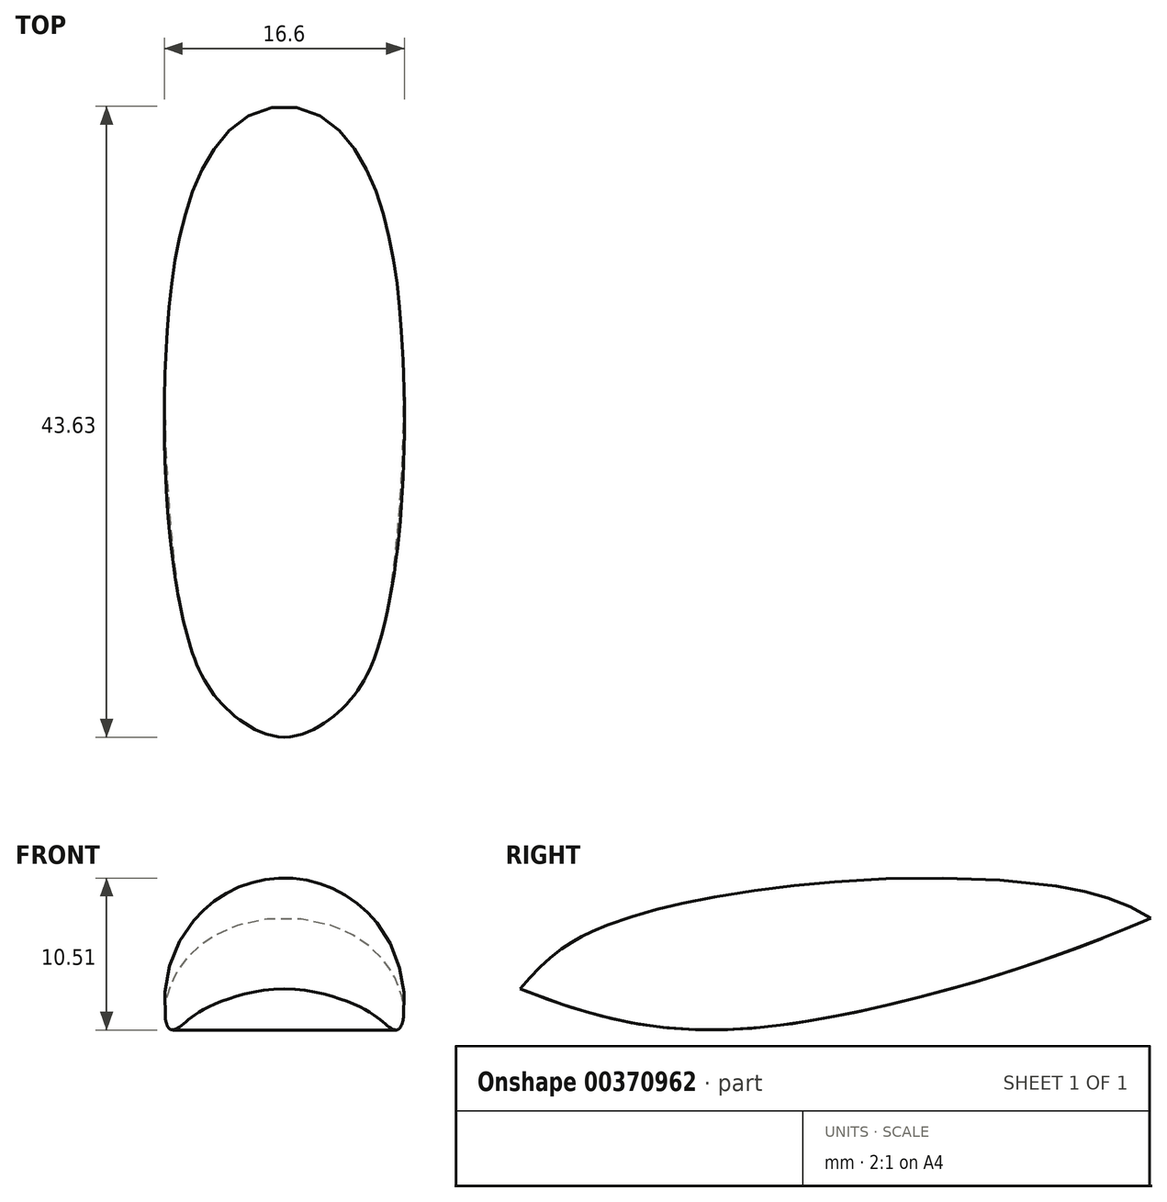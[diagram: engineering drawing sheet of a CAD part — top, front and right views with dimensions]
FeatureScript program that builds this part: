
annotation { "Feature Type Name" : "Feature", "Feature Type Description" : "" }
export const myFeature = defineFeature(function(context is Context, id is Id, definition is map)
    precondition{}
    {
        {
            var Q0;
            Q0=qCreatedBy(makeId("Right.planeOp"),FACE);
            var sketch = newSketch(context, id + "F0", { "sketchPlane" : qUnion([Q0])});
            skLineSegment(sketch, "E0", {"start": v(-61.43, 0) * mm, "end": v(63.71, 0) * mm});
            skLineSegment(sketch, "E1", {"start": v(63.71, 0) * mm, "end": v(63.71, 21.98) * mm});
            skCircle(sketch, "E2", {"center": v(-32.12, 0) * mm, "radius": 12 * mm});
            skCircle(sketch, "E3", {"center": v(39.07, 2) * mm, "radius": 12 * mm});
            skFitSpline(sketch, "E4", {"points": [v(-61.43, 0) * mm, v(-34.2, 19.3) * mm, v(-22.85, 20.07) * mm, v(-9.5, 15.15) * mm, v(4.65, 13.09) * mm, v(29.55, 19.53) * mm, v(44.48, 23.8) * mm, v(63.71, 21.98) * mm], "startDerivative": vector(151.63, 145.86) * mm, "endDerivative": vector(14.11, 0) * mm});
            skSolve(sketch);
        }
        {
            var Q0;
            Q0=qCreatedBy(makeId("Top.planeOp"),FACE);
            cPlane(context, id + "F1", {"entities" : qUnion([Q0]), "cplaneType" : CPlaneType.OFFSET, "offset" : 3 * mm, "width" : 150 * mm, "height" : 150 * mm});
        }
        {
            var Q0;
            {var subQ0=sQuery(id+"F0.wireOp",EDGE,"E1");Q0=makeQuery(id+"F0.imprint","IMPRINT",FACE,{"disambiguationData":[TD([[makeQuery(id+"F0.imprint","IMPRINT",EDGE,{"derivedFrom":subQ0}),1.0]])]});}
            var Q1;
            {var subQ0=sQuery(id+"F0.wireOp",EDGE,"E2");var subQ1=sQuery(id+"F0.wireOp",EDGE,"E0");var subQ2=makeQuery(id+"F0.imprint","INTERSECT",VERTEX,{"disambiguationData":[OD(0.0)],"derivedFrom":[subQ1,subQ0]});Q1=makeQuery(id+"F0.imprint","IMPRINT",FACE,{"disambiguationData":[TD([[makeQuery(id+"F0.imprint","IMPRINT",EDGE,{"disambiguationData":[TD([[subQ2,-1.0]])],"derivedFrom":subQ1}),1.0]])]});}
            var Q2;
            {var subQ0=sQuery(id+"F0.wireOp",EDGE,"E3");var subQ1=sQuery(id+"F0.wireOp",EDGE,"E0");var subQ2=makeQuery(id+"F0.imprint","INTERSECT",VERTEX,{"disambiguationData":[OD(0.0)],"derivedFrom":[subQ1,subQ0]});Q2=makeQuery(id+"F0.imprint","IMPRINT",FACE,{"disambiguationData":[TD([[makeQuery(id+"F0.imprint","IMPRINT",EDGE,{"disambiguationData":[TD([[subQ2,-1.0]])],"derivedFrom":subQ1}),1.0]])]});}
            extrude(context, id + "F2", {"entities" : qUnion([Q0, Q1, Q2]), "endBound" : BoundingType.SYMMETRIC, "depth" : 60 * mm});
        }
        {
            var Q0;
            Q0=qCreatedBy(makeId("Right.planeOp"),FACE);
            var sketch = newSketch(context, id + "F3", { "sketchPlane" : qUnion([Q0])});
            skFitSpline(sketch, "E5", {"points": [v(-15.16, 12.81) * mm, v(-7.29, 19.28) * mm, v(24.33, 23.12) * mm, v(33.89, 18.92) * mm, v(34.04, 16.56) * mm], "startDerivative": vector(49.99, 24.46) * mm, "endDerivative": vector(-2.72, -6.33) * mm});
            skLineSegment(sketch, "E6", {"start": v(-15.16, 12.81) * mm, "end": v(34.15, 16.8) * mm});
            skSolve(sketch);
        }
        {
            var Q0;
            {var subQ0=sQuery(id+"F3.wireOp",EDGE,"E6");var subQ1=sQuery(id+"F3.wireOp",EDGE,"E5");var subQ2=makeQuery(id+"F3.imprint","INTERSECT",VERTEX,{"disambiguationData":[OD(0.0)],"derivedFrom":[subQ1,subQ0]});Q0=makeQuery(id+"F3.imprint","IMPRINT",FACE,{"disambiguationData":[TD([[makeQuery(id+"F3.imprint","IMPRINT",EDGE,{"disambiguationData":[TD([[subQ2,-1.0]])],"derivedFrom":subQ1}),-1.0]])]});}
            var Q1;
            Q1 = qConstructionFilter(qBodyType(qCreatedBy(id + "F3" ,EDGE), BodyType.WIRE), ConstructionObject.NO);
            var Q2;
            Q2=sQuery(id+"F3.wireOp",EDGE,"E6");
            revolve(context, id + "F4", {"operationType" : NewBodyOperationType.ADD, "entities" : qUnion([Q0]), "surfaceEntities" : qUnion([Q1]), "axis" : qUnion([Q2]), "revolveType" : RevolveType.SYMMETRIC, "angle" : 360 * degree});
        }
        {
            var Q0;
            Q0=qCreatedBy(makeId("Right.planeOp"),FACE);
            var sketch = newSketch(context, id + "F5", { "sketchPlane" : qUnion([Q0])});
            skLineSegment(sketch, "E7", {"start": v(-14.66, 16.96) * mm, "end": v(-23.22, 27.93) * mm});
            skLineSegment(sketch, "E8", {"start": v(-23.22, 27.93) * mm, "end": v(-61.74, 13.85) * mm});
            skLineSegment(sketch, "E9", {"start": v(-61.74, 13.85) * mm, "end": v(-57.48, 2.18) * mm});
            skFitSpline(sketch, "E10", {"points": [v(-57.48, 2.18) * mm, v(-36.9, 15.8) * mm, v(-25.53, 18.11) * mm, v(-14.66, 16.96) * mm], "startDerivative": vector(36.14, 27.84) * mm, "endDerivative": vector(35.2, -5.65) * mm});
            skLineSegment(sketch, "E11", {"start": v(34.04, 20.87) * mm, "end": v(39.38, 26.78) * mm});
            skLineSegment(sketch, "E12", {"start": v(39.38, 26.78) * mm, "end": v(68, 24.85) * mm});
            skLineSegment(sketch, "E13", {"start": v(68, 24.85) * mm, "end": v(63.22, 11.9) * mm});
            skFitSpline(sketch, "E14", {"points": [v(34.04, 20.87) * mm, v(45.25, 21.94) * mm, v(58.77, 18.94) * mm, v(63.22, 11.9) * mm], "startDerivative": vector(31.03, 4.85) * mm, "endDerivative": vector(10.27, -27.45) * mm});
            skSolve(sketch);
        }
        {
            var Q0;
            Q0=makeQuery(id+"F5.imprint","IMPRINT",FACE,{"disambiguationData":[TD([[makeQuery(id+"F5.imprint","IMPRINT",EDGE,{"derivedFrom":sQuery(id+"F5.wireOp",EDGE,"E7")}),1.0]])]});
            var Q1;
            Q1=makeQuery(id+"F5.imprint","IMPRINT",FACE,{"disambiguationData":[TD([[makeQuery(id+"F5.imprint","IMPRINT",EDGE,{"derivedFrom":sQuery(id+"F5.wireOp",EDGE,"E11")}),-1.0]])]});
            extrude(context, id + "F6", {"entities" : qUnion([Q0, Q1]), "operationType" : NewBodyOperationType.REMOVE, "endBound" : BoundingType.SYMMETRIC, "oppositeDirection" : true, "depth" : 35 * mm});
        }
        {
            var Q0;
            Q0=makeQuery(id+"F6.boolean.opBoolean","INTERSECT",EDGE,{"derivedFrom":[makeQuery(id+"F2.opExtrude","SWEPT_FACE",FACE,{"disambiguationData":[OSD([sQuery(id+"F0.wireOp",EDGE,"E4")])]}),makeQuery(id+"F6.opExtrude","CAP_FACE",FACE,{"disambiguationData":[OSD([sQuery(id+"F5.wireOp",EDGE,"E7"),sQuery(id+"F5.wireOp",EDGE,"E8"),sQuery(id+"F5.wireOp",EDGE,"E9"),sQuery(id+"F5.wireOp",EDGE,"E10")])],"isStart":false})]});
            var Q1;
            Q1=makeQuery(id+"F6.boolean.opBoolean","INTERSECT",EDGE,{"derivedFrom":[makeQuery(id+"F2.opExtrude","SWEPT_FACE",FACE,{"disambiguationData":[OSD([sQuery(id+"F0.wireOp",EDGE,"E4")])]}),makeQuery(id+"F6.opExtrude","CAP_FACE",FACE,{"disambiguationData":[OSD([sQuery(id+"F5.wireOp",EDGE,"E7"),sQuery(id+"F5.wireOp",EDGE,"E8"),sQuery(id+"F5.wireOp",EDGE,"E9"),sQuery(id+"F5.wireOp",EDGE,"E10")])],"isStart":true})]});
            var Q2;
            Q2=makeQuery(id+"F6.boolean.opBoolean","INTERSECT",EDGE,{"derivedFrom":[makeQuery(id+"F2.opExtrude","SWEPT_FACE",FACE,{"disambiguationData":[OSD([sQuery(id+"F0.wireOp",EDGE,"E4")])]}),makeQuery(id+"F6.opExtrude","SWEPT_FACE",FACE,{"disambiguationData":[OSD([sQuery(id+"F5.wireOp",EDGE,"E9")])]})]});
            var Q3;
            Q3=makeQuery(id+"F6.boolean.opBoolean","INTERSECT",EDGE,{"disambiguationData":[OD(0.0)],"derivedFrom":[makeQuery(id+"F2.opExtrude","SWEPT_FACE",FACE,{"disambiguationData":[OSD([sQuery(id+"F0.wireOp",EDGE,"E4")])]}),makeQuery(id+"F6.opExtrude","SWEPT_FACE",FACE,{"disambiguationData":[OSD([sQuery(id+"F5.wireOp",EDGE,"E7")])]})]});
            var Q4;
            Q4=makeQuery(id+"F6.boolean.opBoolean","INTERSECT",EDGE,{"disambiguationData":[OD(1.0)],"derivedFrom":[makeQuery(id+"F2.opExtrude","SWEPT_FACE",FACE,{"disambiguationData":[OSD([sQuery(id+"F0.wireOp",EDGE,"E4")])]}),makeQuery(id+"F6.opExtrude","SWEPT_FACE",FACE,{"disambiguationData":[OSD([sQuery(id+"F5.wireOp",EDGE,"E7")])]})]});
            var Q5;
            Q5=makeQuery(id+"F2.opExtrude","CAP_EDGE",EDGE,{"disambiguationData":[OSD([sQuery(id+"F0.wireOp",EDGE,"E4")])],"isStart":true});
            var Q6;
            Q6=makeQuery(id+"F2.opExtrude","CAP_EDGE",EDGE,{"disambiguationData":[OSD([sQuery(id+"F0.wireOp",EDGE,"E4")])],"isStart":false});
            var Q7;
            Q7=makeQuery(id+"F6.boolean.opBoolean","INTERSECT",EDGE,{"derivedFrom":[makeQuery(id+"F2.opExtrude","SWEPT_FACE",FACE,{"disambiguationData":[OSD([sQuery(id+"F0.wireOp",EDGE,"E4")])]}),makeQuery(id+"F6.opExtrude","CAP_FACE",FACE,{"disambiguationData":[OSD([sQuery(id+"F5.wireOp",EDGE,"E11"),sQuery(id+"F5.wireOp",EDGE,"E12"),sQuery(id+"F5.wireOp",EDGE,"E13"),sQuery(id+"F5.wireOp",EDGE,"E14")])],"isStart":false})]});
            var Q8;
            Q8=makeQuery(id+"F6.boolean.opBoolean","INTERSECT",EDGE,{"derivedFrom":[makeQuery(id+"F2.opExtrude","SWEPT_FACE",FACE,{"disambiguationData":[OSD([sQuery(id+"F0.wireOp",EDGE,"E4")])]}),makeQuery(id+"F6.opExtrude","SWEPT_FACE",FACE,{"disambiguationData":[OSD([sQuery(id+"F5.wireOp",EDGE,"E11")])]})]});
            var Q9;
            Q9=makeQuery(id+"F6.boolean.opBoolean","INTERSECT",EDGE,{"derivedFrom":[makeQuery(id+"F2.opExtrude","SWEPT_FACE",FACE,{"disambiguationData":[OSD([sQuery(id+"F0.wireOp",EDGE,"E4")])]}),makeQuery(id+"F6.opExtrude","CAP_FACE",FACE,{"disambiguationData":[OSD([sQuery(id+"F5.wireOp",EDGE,"E11"),sQuery(id+"F5.wireOp",EDGE,"E12"),sQuery(id+"F5.wireOp",EDGE,"E13"),sQuery(id+"F5.wireOp",EDGE,"E14")])],"isStart":true})]});
            var Q10;
            Q10=makeQuery(id+"F6.boolean.opBoolean","INTERSECT",EDGE,{"derivedFrom":[makeQuery(id+"F2.opExtrude","SWEPT_FACE",FACE,{"disambiguationData":[OSD([sQuery(id+"F0.wireOp",EDGE,"E1")])]}),makeQuery(id+"F6.opExtrude","CAP_FACE",FACE,{"disambiguationData":[OSD([sQuery(id+"F5.wireOp",EDGE,"E11"),sQuery(id+"F5.wireOp",EDGE,"E12"),sQuery(id+"F5.wireOp",EDGE,"E13"),sQuery(id+"F5.wireOp",EDGE,"E14")])],"isStart":true})]});
            var Q11;
            Q11=makeQuery(id+"F6.boolean.opBoolean","INTERSECT",EDGE,{"derivedFrom":[makeQuery(id+"F2.opExtrude","SWEPT_FACE",FACE,{"disambiguationData":[OSD([sQuery(id+"F0.wireOp",EDGE,"E1")])]}),makeQuery(id+"F6.opExtrude","SWEPT_FACE",FACE,{"disambiguationData":[OSD([sQuery(id+"F5.wireOp",EDGE,"E14")])]})]});
            var Q12;
            Q12=makeQuery(id+"F6.boolean.opBoolean","INTERSECT",EDGE,{"derivedFrom":[makeQuery(id+"F2.opExtrude","SWEPT_FACE",FACE,{"disambiguationData":[OSD([sQuery(id+"F0.wireOp",EDGE,"E1")])]}),makeQuery(id+"F6.opExtrude","CAP_FACE",FACE,{"disambiguationData":[OSD([sQuery(id+"F5.wireOp",EDGE,"E11"),sQuery(id+"F5.wireOp",EDGE,"E12"),sQuery(id+"F5.wireOp",EDGE,"E13"),sQuery(id+"F5.wireOp",EDGE,"E14")])],"isStart":false})]});
            var Q13;
            {var subQ0=sQuery(id+"F0.wireOp",EDGE,"E4");var subQ1=sQuery(id+"F0.wireOp",EDGE,"E1");Q13=makeQuery(id+"F6.boolean.opBoolean","SPLIT",EDGE,{"disambiguationData":[TD([makeQuery(id+"F2.opExtrude","CAP_FACE",FACE,{"disambiguationData":[OSD([sQuery(id+"F0.wireOp",EDGE,"E0"),subQ1,subQ0])],"isStart":true})])],"derivedFrom":makeQuery(id+"F2.opExtrude","SWEPT_EDGE",EDGE,{"disambiguationData":[OSD([subQ1,subQ0])]})});}
            var Q14;
            Q14=makeQuery(id+"F2.opExtrude","CAP_EDGE",EDGE,{"disambiguationData":[OSD([sQuery(id+"F0.wireOp",EDGE,"E1")])],"isStart":true});
            var Q15;
            Q15=makeQuery(id+"F2.opExtrude","CAP_EDGE",EDGE,{"disambiguationData":[OSD([sQuery(id+"F0.wireOp",EDGE,"E1")])],"isStart":false});
            fillet(context, id + "F7", {"entities" : qUnion([Q0, Q1, Q2, Q3, Q4, Q5, Q6, Q7, Q8, Q9, Q10, Q11, Q12, Q13, Q14, Q15]), "radius" : 1 * mm, "tangentPropagation" : true, "allowEdgeOverflow" : false});
        }
        {
            var Q0;
            {var subQ0=sQuery(id+"F0.wireOp",EDGE,"E2");var subQ1=sQuery(id+"F0.wireOp",EDGE,"E0");var subQ2=makeQuery(id+"F0.imprint","INTERSECT",VERTEX,{"disambiguationData":[OD(0.0)],"derivedFrom":[subQ1,subQ0]});Q0=makeQuery(id+"F0.imprint","IMPRINT",FACE,{"disambiguationData":[TD([[makeQuery(id+"F0.imprint","IMPRINT",EDGE,{"disambiguationData":[TD([[subQ2,-1.0]])],"derivedFrom":subQ1}),1.0]])]});}
            var Q1;
            {var subQ0=sQuery(id+"F0.wireOp",EDGE,"E3");var subQ1=sQuery(id+"F0.wireOp",EDGE,"E0");var subQ2=makeQuery(id+"F0.imprint","INTERSECT",VERTEX,{"disambiguationData":[OD(0.0)],"derivedFrom":[subQ1,subQ0]});Q1=makeQuery(id+"F0.imprint","IMPRINT",FACE,{"disambiguationData":[TD([[makeQuery(id+"F0.imprint","IMPRINT",EDGE,{"disambiguationData":[TD([[subQ2,-1.0]])],"derivedFrom":subQ1}),1.0]])]});}
            extrude(context, id + "F8", {"entities" : qUnion([Q0, Q1]), "operationType" : NewBodyOperationType.REMOVE, "endBound" : BoundingType.SYMMETRIC, "oppositeDirection" : true, "depth" : 60 * mm});
        }
    });
